# Revit family: FU_Chair_Sandler_Ring
name_source: partatom
category: Furniture
units: mm (PartAtom-declared; Revit-internal decimal feet)

## family parameters
Always vertical = Yes
Cut with Voids When Loaded = No
OmniClass Number = 23.40.20.00
OmniClass Title = General Furniture and Specialties
Room Calculation Point = No
Shared = No
Work Plane-Based = No

## types (2) — shared parameters
Depth = 520 mm  [stored 1.70604 ft]
Frame = Metal - Chrome - Polished
Height = 780 mm  [stored 2.55906 ft]
Manufacturer = Sandler
Seat = Fabric - Gravity - Wheat CPC21
URL = https://www.sandlerseating.com
Width = 520 mm  [stored 1.70604 ft]
zero-valued in all types: Default Elevation

## per-type parameters (varying)
| type | Description | IsVisible |
| Ring 1.1 | Upholstered side chair on steel frame. | No |
| Ring 2.1 | Upholstered armchair on steel frame. | Yes |

note: column(s) folded — value = type name in every type: Model

note: [stored X ft] marks values corroborated as IEEE doubles in the binary element streams (Revit-internal decimal feet)

## geometry (parser evidence)
native form markers: Sweep x4
no freeform markers — native parametric forms only
